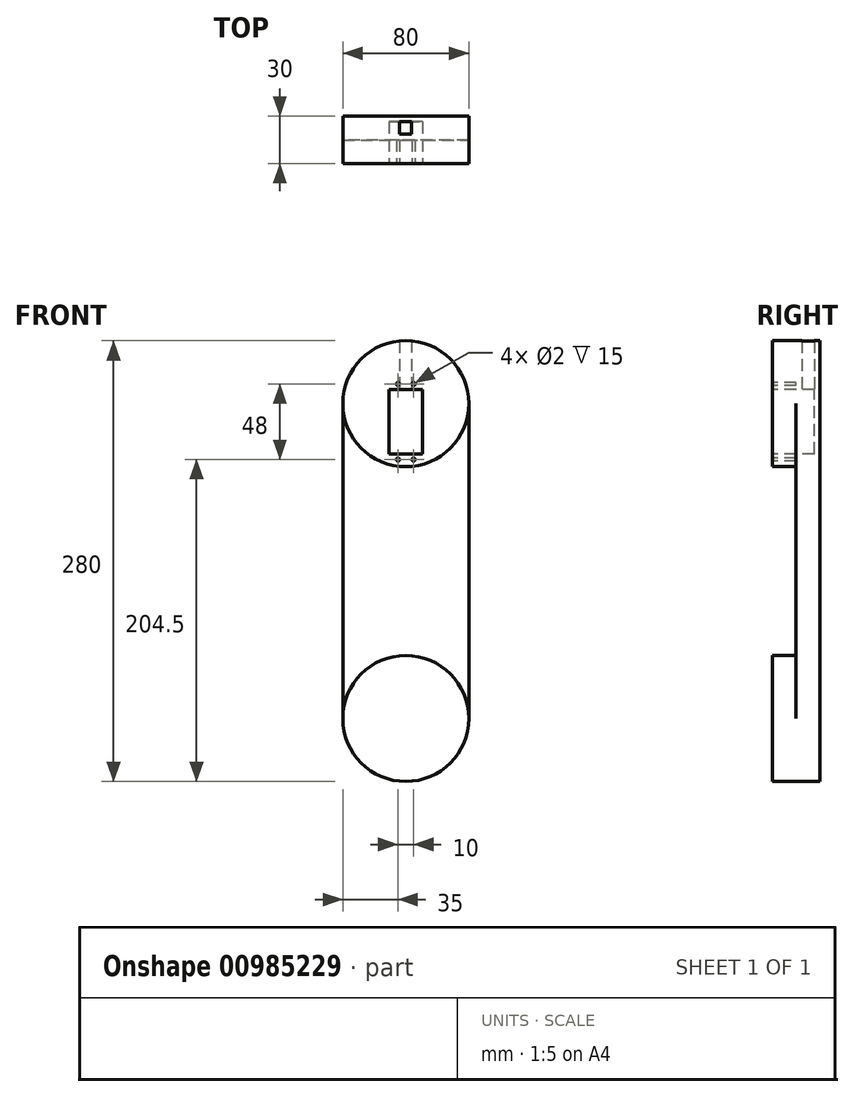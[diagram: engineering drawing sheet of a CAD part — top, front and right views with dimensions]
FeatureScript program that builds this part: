
annotation { "Feature Type Name" : "Feature", "Feature Type Description" : "" }
export const myFeature = defineFeature(function(context is Context, id is Id, definition is map)
    precondition{}
    {
        {
            var Q0;
            Q0=qCreatedBy(makeId("Front.planeOp"),FACE);
            var sketch = newSketch(context, id + "F0", { "sketchPlane" : qUnion([Q0])});
            skCircle(sketch, "E0", {"center": v(0, 0) * mm, "radius": 40 * mm});
            skCircle(sketch, "E1", {"center": v(0, 200) * mm, "radius": 40 * mm});
            skLineSegment(sketch, "E2", {"start": v(-40, 200) * mm, "end": v(-40, 0) * mm});
            skLineSegment(sketch, "E3", {"start": v(40, 200) * mm, "end": v(40, 0) * mm});
            skSolve(sketch);
        }
        {
            var Q0;
            {var subQ0=sQuery(id+"F0.wireOp",EDGE,"E2");Q0=makeQuery(id+"F0.imprint","IMPRINT",FACE,{"disambiguationData":[TD([[makeQuery(id+"F0.imprint","IMPRINT",EDGE,{"derivedFrom":subQ0}),1.0]])]});}
            var Q1;
            {var subQ0=sQuery(id+"F0.wireOp",EDGE,"E1");var subQ1=makeQuery(id+"F0.imprint","INTERSECT",VERTEX,{"derivedFrom":[subQ0,sQuery(id+"F0.wireOp",EDGE,"E2")]});Q1=makeQuery(id+"F0.imprint","IMPRINT",FACE,{"disambiguationData":[TD([[makeQuery(id+"F0.imprint","IMPRINT",EDGE,{"disambiguationData":[TD([[subQ1,1.0]])],"derivedFrom":subQ0}),1.0]])]});}
            var Q2;
            {var subQ0=sQuery(id+"F0.wireOp",EDGE,"E0");var subQ1=makeQuery(id+"F0.imprint","INTERSECT",VERTEX,{"derivedFrom":[subQ0,sQuery(id+"F0.wireOp",EDGE,"E2")]});Q2=makeQuery(id+"F0.imprint","IMPRINT",FACE,{"disambiguationData":[TD([[makeQuery(id+"F0.imprint","IMPRINT",EDGE,{"disambiguationData":[TD([[subQ1,1.0]])],"derivedFrom":subQ0}),1.0]])]});}
            extrude(context, id + "F1", {"entities" : qUnion([Q0, Q1, Q2]), "oppositeDirection" : true, "depth" : 15 * mm, "offsetDistance" : 25 * mm});
        }
        {
            var Q0;
            {var subQ0=sQuery(id+"F0.wireOp",EDGE,"E1");var subQ1=makeQuery(id+"F0.imprint","INTERSECT",VERTEX,{"derivedFrom":[subQ0,sQuery(id+"F0.wireOp",EDGE,"E2")]});Q0=makeQuery(id+"F0.imprint","IMPRINT",FACE,{"disambiguationData":[TD([[makeQuery(id+"F0.imprint","IMPRINT",EDGE,{"disambiguationData":[TD([[subQ1,1.0]])],"derivedFrom":subQ0}),1.0]])]});}
            extrude(context, id + "F2", {"entities" : qUnion([Q0]), "operationType" : NewBodyOperationType.ADD, "depth" : 15 * mm, "offsetDistance" : 25 * mm});
        }
        {
            var Q0;
            {var subQ0=sQuery(id+"F0.wireOp",EDGE,"E0");var subQ1=makeQuery(id+"F0.imprint","INTERSECT",VERTEX,{"derivedFrom":[subQ0,sQuery(id+"F0.wireOp",EDGE,"E2")]});Q0=makeQuery(id+"F0.imprint","IMPRINT",FACE,{"disambiguationData":[TD([[makeQuery(id+"F0.imprint","IMPRINT",EDGE,{"disambiguationData":[TD([[subQ1,1.0]])],"derivedFrom":subQ0}),1.0]])]});}
            extrude(context, id + "F3", {"entities" : qUnion([Q0]), "operationType" : NewBodyOperationType.ADD, "depth" : 15 * mm, "offsetDistance" : 25 * mm});
        }
        {
            var Q0;
            Q0=makeQuery(id+"F2.opExtrude","CAP_FACE",FACE,{"disambiguationData":[OSD([sQuery(id+"F0.wireOp",EDGE,"E1")])],"isStart":false});
            var sketch = newSketch(context, id + "F4", { "sketchPlane" : qUnion([Q0])});
            skLineSegment(sketch, "E4", {"start": v(10.5, 209) * mm, "end": v(-10.5, 209) * mm});
            skLineSegment(sketch, "E5", {"start": v(-10.5, 209) * mm, "end": v(-10.5, 168) * mm});
            skLineSegment(sketch, "E6", {"start": v(-10.5, 168) * mm, "end": v(10.5, 168) * mm});
            skLineSegment(sketch, "E7", {"start": v(10.5, 168) * mm, "end": v(10.5, 209) * mm});
            skSolve(sketch);
        }
        {
            var Q0;
            Q0=makeQuery(id+"F4.imprint","IMPRINT",FACE,{"disambiguationData":[TD([[makeQuery(id+"F4.imprint","IMPRINT",EDGE,{"derivedFrom":sQuery(id+"F4.wireOp",EDGE,"E4")}),1.0]])]});
            extrude(context, id + "F5", {"entities" : qUnion([Q0]), "operationType" : NewBodyOperationType.REMOVE, "oppositeDirection" : true, "depth" : 26.6 * mm, "offsetDistance" : 25 * mm});
        }
        {
            var Q0;
            Q0=makeQuery(id+"F2.opExtrude","CAP_FACE",FACE,{"disambiguationData":[OSD([sQuery(id+"F0.wireOp",EDGE,"E1")])],"isStart":false});
            var sketch = newSketch(context, id + "F6", { "sketchPlane" : qUnion([Q0])});
            skCircle(sketch, "E8", {"center": v(-5, 212.5) * mm, "radius": 1 * mm});
            skCircle(sketch, "E9", {"center": v(5, 212.5) * mm, "radius": 1 * mm});
            skCircle(sketch, "E10", {"center": v(-5, 164.5) * mm, "radius": 1 * mm});
            skCircle(sketch, "E11", {"center": v(5, 164.5) * mm, "radius": 1 * mm});
            skSolve(sketch);
        }
        {
            var Q0;
            Q0=makeQuery(id+"F6.imprint","IMPRINT",FACE,{"disambiguationData":[TD([[makeQuery(id+"F6.imprint","IMPRINT",EDGE,{"derivedFrom":sQuery(id+"F6.wireOp",EDGE,"E8")}),1.0]])]});
            var Q1;
            Q1=makeQuery(id+"F6.imprint","IMPRINT",FACE,{"disambiguationData":[TD([[makeQuery(id+"F6.imprint","IMPRINT",EDGE,{"derivedFrom":sQuery(id+"F6.wireOp",EDGE,"E9")}),1.0]])]});
            var Q2;
            Q2=makeQuery(id+"F6.imprint","IMPRINT",FACE,{"disambiguationData":[TD([[makeQuery(id+"F6.imprint","IMPRINT",EDGE,{"derivedFrom":sQuery(id+"F6.wireOp",EDGE,"E11")}),1.0]])]});
            var Q3;
            Q3=makeQuery(id+"F6.imprint","IMPRINT",FACE,{"disambiguationData":[TD([[makeQuery(id+"F6.imprint","IMPRINT",EDGE,{"derivedFrom":sQuery(id+"F6.wireOp",EDGE,"E10")}),1.0]])]});
            extrude(context, id + "F7", {"entities" : qUnion([Q0, Q1, Q2, Q3]), "operationType" : NewBodyOperationType.REMOVE, "oppositeDirection" : true, "depth" : 15 * mm, "offsetDistance" : 25 * mm});
        }
        {
            var Q0;
            Q0=makeQuery(id+"F5.boolean.opBoolean","COPY",FACE,{"derivedFrom":makeQuery(id+"F5.opExtrude","SWEPT_FACE",FACE,{"disambiguationData":[OSD([sQuery(id+"F4.wireOp",EDGE,"E4")])]})});
            var sketch = newSketch(context, id + "F8", { "sketchPlane" : qUnion([Q0])});
            skLineSegment(sketch, "E12.bottom", {"start": v(-4, -11.6) * mm, "end": v(3.5, -11.6) * mm});
            skLineSegment(sketch, "E12.top", {"start": v(-4, -3.6) * mm, "end": v(3.5, -3.6) * mm});
            skLineSegment(sketch, "E12.left", {"start": v(-4, -11.6) * mm, "end": v(-4, -3.6) * mm});
            skLineSegment(sketch, "E12.right", {"start": v(3.5, -11.6) * mm, "end": v(3.5, -3.6) * mm});
            skSolve(sketch);
        }
        {
            var Q0;
            Q0 = qSketchRegion(id + "F8", true);
            extrude(context, id + "F9", {"entities" : qUnion([Q0]), "operationType" : NewBodyOperationType.REMOVE, "endBound" : BoundingType.UP_TO_NEXT, "oppositeDirection" : true, "depth" : 25 * mm, "offsetDistance" : 25 * mm});
        }
    });
